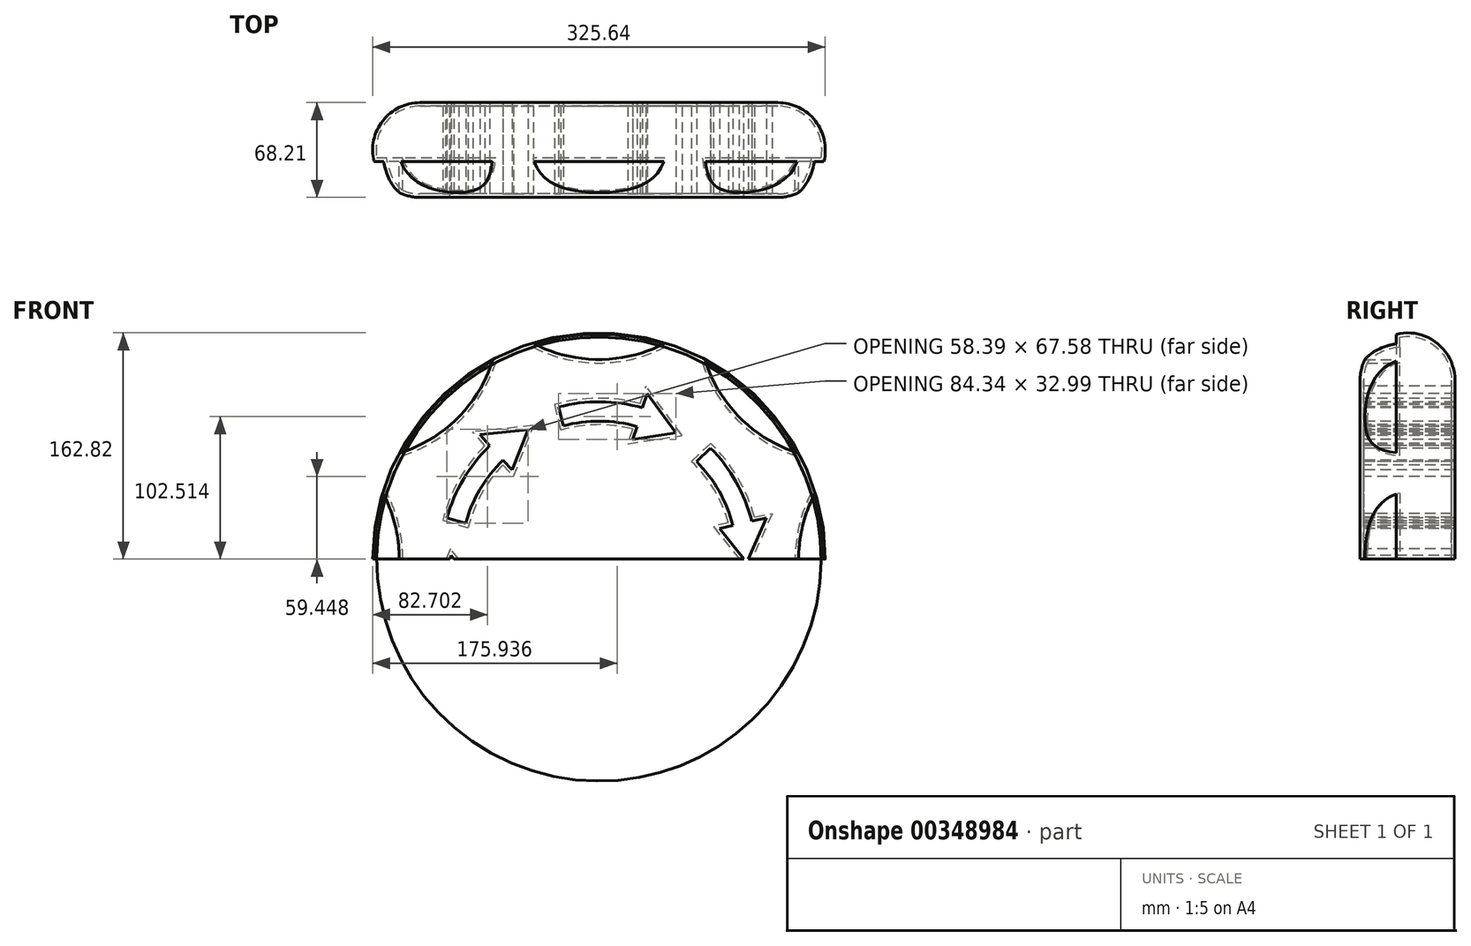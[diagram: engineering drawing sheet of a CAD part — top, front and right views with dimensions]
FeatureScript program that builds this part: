
annotation { "Feature Type Name" : "Feature", "Feature Type Description" : "" }
export const myFeature = defineFeature(function(context is Context, id is Id, definition is map)
    precondition{}
    {
        {
            var Q0;
            Q0=qCreatedBy(makeId("Right.planeOp"),FACE);
            var sketch = newSketch(context, id + "F0", { "sketchPlane" : qUnion([Q0])});
            skLineSegment(sketch, "E0", {"start": v(-32.22, 0) * mm, "end": v(-32.22, 128.71) * mm});
            skLineSegment(sketch, "E1", {"start": v(36, 128.71) * mm, "end": v(36, 0) * mm});
            skArc(sketch, "E2", {"start": v(36, 128.71) * mm, "mid": v(1.89, 162.82) * mm, "end": v(-32.22, 128.71) * mm});
            skLineSegment(sketch, "E3", {"start": v(-136.39, 0) * mm, "end": v(115.3, 0) * mm, "construction": true});
            skLineSegment(sketch, "E4", {"start": v(0, -151.18) * mm, "end": v(1.89, 219.16) * mm, "construction": true});
            skPoint(sketch, "E4.endSnap0", {"position": v(1.89, 162.82) * mm});
            skLineSegment(sketch, "E5", {"start": v(-32.22, 0) * mm, "end": v(36, 0) * mm});
            skSolve(sketch);
        }
        {
            var Q0;
            Q0=makeQuery(id+"F0.imprint","IMPRINT",FACE,{"disambiguationData":[TD([[makeQuery(id+"F0.imprint","IMPRINT",EDGE,{"derivedFrom":sQuery(id+"F0.wireOp",EDGE,"E0")}),-1.0]])]});
            var Q1;
            Q1=sQuery(id+"F0.wireOp",EDGE,"E2");
            var Q2;
            Q2=sQuery(id+"F0.wireOp",EDGE,"E1");
            var Q3;
            Q3=sQuery(id+"F0.wireOp",EDGE,"E0");
            var Q4;
            Q4=sQuery(id+"F0.wireOp",EDGE,"E5");
            var Q5;
            Q5=sQuery(id+"F0.wireOp",EDGE,"E3");
            revolve(context, id + "F1", {"entities" : qUnion([Q0]), "surfaceEntities" : qUnion([Q1, Q2, Q3, Q4]), "axis" : qUnion([Q5]), "revolveType" : RevolveType.FULL});
        }
        {
            var Q0;
            Q0=qCreatedBy(makeId("Front.planeOp"),FACE);
            cPlane(context, id + "F2", {"entities" : qUnion([Q0]), "cplaneType" : CPlaneType.OFFSET, "offset" : 6.35 * mm, "width" : 152.4 * mm, "height" : 152.4 * mm});
        }
        {
            var Q0;
            Q0=qCreatedBy(id+"F2.planeOp",FACE);
            var sketch = newSketch(context, id + "F3", { "sketchPlane" : qUnion([Q0])});
            skCircle(sketch, "E6", {"center": v(0, 245.45) * mm, "radius": 101.8 * mm});
            skSolve(sketch);
        }
        {
            var Q0;
            Q0 = qSketchRegion(id + "F3", true);
            extrude(context, id + "F4", {"entities" : qUnion([Q0]), "depth" : 75.8 * mm});
        }
        {
            var Q0;
            Q0=makeQuery(id+"F4.opExtrude","SWEPT_BODY",BODY,{"disambiguationData":[OSD([sQuery(id+"F3.wireOp",EDGE,"E6")])]});
            var Q1;
            Q1=sQuery(id+"F0.wireOp",EDGE,"E3");
            var Q2;
            Q2=makeQuery(id+"F1.opRevolve","SWEPT_BODY",BODY,{"disambiguationData":[OSD([sQuery(id+"F0.wireOp",EDGE,"E0"),sQuery(id+"F0.wireOp",EDGE,"E1"),sQuery(id+"F0.wireOp",EDGE,"E2"),sQuery(id+"F0.wireOp",EDGE,"E5")])]});
            circularPattern(context, id + "F5", {"operationType" : NewBodyOperationType.REMOVE, "entities" : qUnion([Q0]), "axis" : qUnion([Q1]), "angle" : 360 * degree, "instanceCount" : 8, "equalSpace" : true});
        }
        {
            var Q0;
            Q0=makeQuery(id+"F1.opRevolve","SWEPT_FACE",FACE,{"disambiguationData":[OSD([sQuery(id+"F0.wireOp",EDGE,"E0")])]});
            var sketch = newSketch(context, id + "F6", { "sketchPlane" : qUnion([Q0])});
            skCircle(sketch, "E7", {"center": v(0, 0) * mm, "radius": 87.53 * mm});
            skCircle(sketch, "E8", {"center": v(0, 0) * mm, "radius": 106.24 * mm, "construction": true});
            skArc(sketch, "E9.0", {"start": v(-31.34, -108.82) * mm, "mid": v(-1.19, -113.23) * mm, "end": v(29.05, -109.45) * mm});
            skArc(sketch, "E10.0", {"start": v(-27.26, -95.42) * mm, "mid": v(-0.8, -99.24) * mm, "end": v(25.71, -95.85) * mm});
            skLineSegment(sketch, "E11", {"start": v(29.05, -109.45) * mm, "end": v(25.71, -95.85) * mm});
            skLineSegment(sketch, "E12", {"start": v(-31.34, -108.82) * mm, "end": v(-34.69, -119) * mm});
            skLineSegment(sketch, "E13", {"start": v(-27.26, -95.42) * mm, "end": v(-24.31, -86.02) * mm});
            skLineSegment(sketch, "E14", {"start": v(-24.31, -86.02) * mm, "end": v(-24.31, -86.02) * mm});
            skLineSegment(sketch, "E15", {"start": v(-24.31, -86.02) * mm, "end": v(-55.29, -90.72) * mm});
            skPoint(sketch, "E15.endSnap0", {"position": v(-25.79, -90.72) * mm});
            skLineSegment(sketch, "E16", {"start": v(-55.29, -90.72) * mm, "end": v(-34.69, -119) * mm});
            skSolve(sketch);
        }
        {
            var Q0;
            Q0=makeQuery(id+"F6.imprint","IMPRINT",FACE,{"disambiguationData":[TD([[makeQuery(id+"F6.imprint","IMPRINT",EDGE,{"derivedFrom":sQuery(id+"F6.wireOp",EDGE,"E9.0")}),1.0]])]});
            extrude(context, id + "F7", {"entities" : qUnion([Q0]), "oppositeDirection" : true, "depth" : 139.47 * mm});
        }
        {
            var Q0;
            Q0=makeQuery(id+"F7.opExtrude","SWEPT_BODY",BODY,{"disambiguationData":[OSD([sQuery(id+"F6.wireOp",EDGE,"E9.0"),sQuery(id+"F6.wireOp",EDGE,"E10.0"),sQuery(id+"F6.wireOp",EDGE,"E11"),sQuery(id+"F6.wireOp",EDGE,"E12"),sQuery(id+"F6.wireOp",EDGE,"E13"),sQuery(id+"F6.wireOp",EDGE,"E15"),sQuery(id+"F6.wireOp",EDGE,"E16")])]});
            var Q1;
            Q1=sQuery(id+"F0.wireOp",EDGE,"E3");
            var Q2;
            Q2=makeQuery(id+"F1.opRevolve","SWEPT_BODY",BODY,{"disambiguationData":[OSD([sQuery(id+"F0.wireOp",EDGE,"E0"),sQuery(id+"F0.wireOp",EDGE,"E1"),sQuery(id+"F0.wireOp",EDGE,"E2"),sQuery(id+"F0.wireOp",EDGE,"E5")])]});
            circularPattern(context, id + "F8", {"operationType" : NewBodyOperationType.REMOVE, "entities" : qUnion([Q0]), "axis" : qUnion([Q1]), "angle" : 360 * degree, "instanceCount" : 6, "equalSpace" : true});
        }
        {
            var Q0;
            Q0=qCreatedBy(makeId("Top.planeOp"),FACE);
            var sketch = newSketch(context, id + "F9", { "sketchPlane" : qUnion([Q0])});
            skLineSegment(sketch, "E17.bottom", {"start": v(224.5, 58.72) * mm, "end": v(-224.5, 58.72) * mm});
            skLineSegment(sketch, "E17.top", {"start": v(224.5, -58.72) * mm, "end": v(-224.5, -58.72) * mm});
            skLineSegment(sketch, "E17.left", {"start": v(224.5, 58.72) * mm, "end": v(224.5, -58.72) * mm});
            skLineSegment(sketch, "E17.right", {"start": v(-224.5, 58.72) * mm, "end": v(-224.5, -58.72) * mm});
            skPoint(sketch, "E17.middle", {"position": v(0, 0) * mm});
            skSolve(sketch);
        }
        {
            var Q0;
            Q0 = qSketchRegion(id + "F9", true);
            extrude(context, id + "F10", {"entities" : qUnion([Q0]), "operationType" : NewBodyOperationType.REMOVE, "oppositeDirection" : true, "depth" : 209.86 * mm});
        }
        {
            var Q0;
            {var subQ0=sQuery(id+"F6.wireOp",EDGE,"E15");var subQ1=makeQuery(id+"F7.opExtrude","SWEPT_FACE",FACE,{"disambiguationData":[OSD([subQ0])]});Q0=makeQuery(id+"F10.boolean.opBoolean","COPY",FACE,{"disambiguationData":[TD([makeQuery(id+"F8.boolean.opBoolean","COPY",FACE,{"derivedFrom":makeQuery(id+"F8.opPattern","COPY",FACE,{"derivedFrom":subQ1,"instanceName":"1"})})])],"derivedFrom":makeQuery(id+"F10.opExtrude","CAP_FACE",FACE,{"disambiguationData":[OSD([sQuery(id+"F9.wireOp",EDGE,"E17.bottom"),sQuery(id+"F9.wireOp",EDGE,"E17.top"),sQuery(id+"F9.wireOp",EDGE,"E17.left"),sQuery(id+"F9.wireOp",EDGE,"E17.right")])],"isStart":true})});}
            var Q1;
            {var subQ0=sQuery(id+"F3.wireOp",EDGE,"E6");Q1=makeQuery(id+"F10.boolean.opBoolean","COPY",FACE,{"disambiguationData":[TD([makeQuery(id+"F5.boolean.opBoolean","COPY",FACE,{"derivedFrom":makeQuery(id+"F5.opPattern","COPY",FACE,{"derivedFrom":makeQuery(id+"F4.opExtrude","SWEPT_FACE",FACE,{"disambiguationData":[OSD([subQ0])]}),"instanceName":"6"})})])],"derivedFrom":makeQuery(id+"F10.opExtrude","CAP_FACE",FACE,{"disambiguationData":[OSD([sQuery(id+"F9.wireOp",EDGE,"E17.bottom"),sQuery(id+"F9.wireOp",EDGE,"E17.top"),sQuery(id+"F9.wireOp",EDGE,"E17.left"),sQuery(id+"F9.wireOp",EDGE,"E17.right")])],"isStart":true})});}
            var Q2;
            {var subQ0=sQuery(id+"F3.wireOp",EDGE,"E6");Q2=makeQuery(id+"F10.boolean.opBoolean","COPY",FACE,{"disambiguationData":[TD([makeQuery(id+"F5.boolean.opBoolean","COPY",FACE,{"derivedFrom":makeQuery(id+"F5.opPattern","COPY",FACE,{"derivedFrom":makeQuery(id+"F4.opExtrude","SWEPT_FACE",FACE,{"disambiguationData":[OSD([subQ0])]}),"instanceName":"2"})})])],"derivedFrom":makeQuery(id+"F10.opExtrude","CAP_FACE",FACE,{"disambiguationData":[OSD([sQuery(id+"F9.wireOp",EDGE,"E17.bottom"),sQuery(id+"F9.wireOp",EDGE,"E17.top"),sQuery(id+"F9.wireOp",EDGE,"E17.left"),sQuery(id+"F9.wireOp",EDGE,"E17.right")])],"isStart":true})});}
            shell(context, id + "F11", {"entities" : qUnion([Q0, Q1, Q2]), "thickness" : 2.5 * mm});
        }
    });
